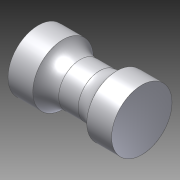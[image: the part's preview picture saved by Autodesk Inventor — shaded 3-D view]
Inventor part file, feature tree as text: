
AUTODESK INVENTOR PART (.ipt)
format: ipt  version: 2012 (Build 160160000, 160)  size: 119,296 bytes
history: native  units: mm
features: extrude x2, sketch x1, fillet x1
ambient origin geometry x8: Origin, YZ Plane, XZ Plane, XY Plane, X Axis, Y Axis, Z Axis, Center Point
bodies: Solid1 (feature_tree)
feature tree (4):
  sketch  "Sketch2"  dims[d0=5.6mm d1=4.0mm d2=9.6mm d3=0.0mm d4=5.0mm d5=0.0mm d6=2.0mm]
  extrude  "Extrusion1"  Depth=4.0mm
  extrude  "Extrusion2"  Depth=9.6mm TaperAngle=0.0deg
  fillet  "Fillet1"  Radius=5.0mm
